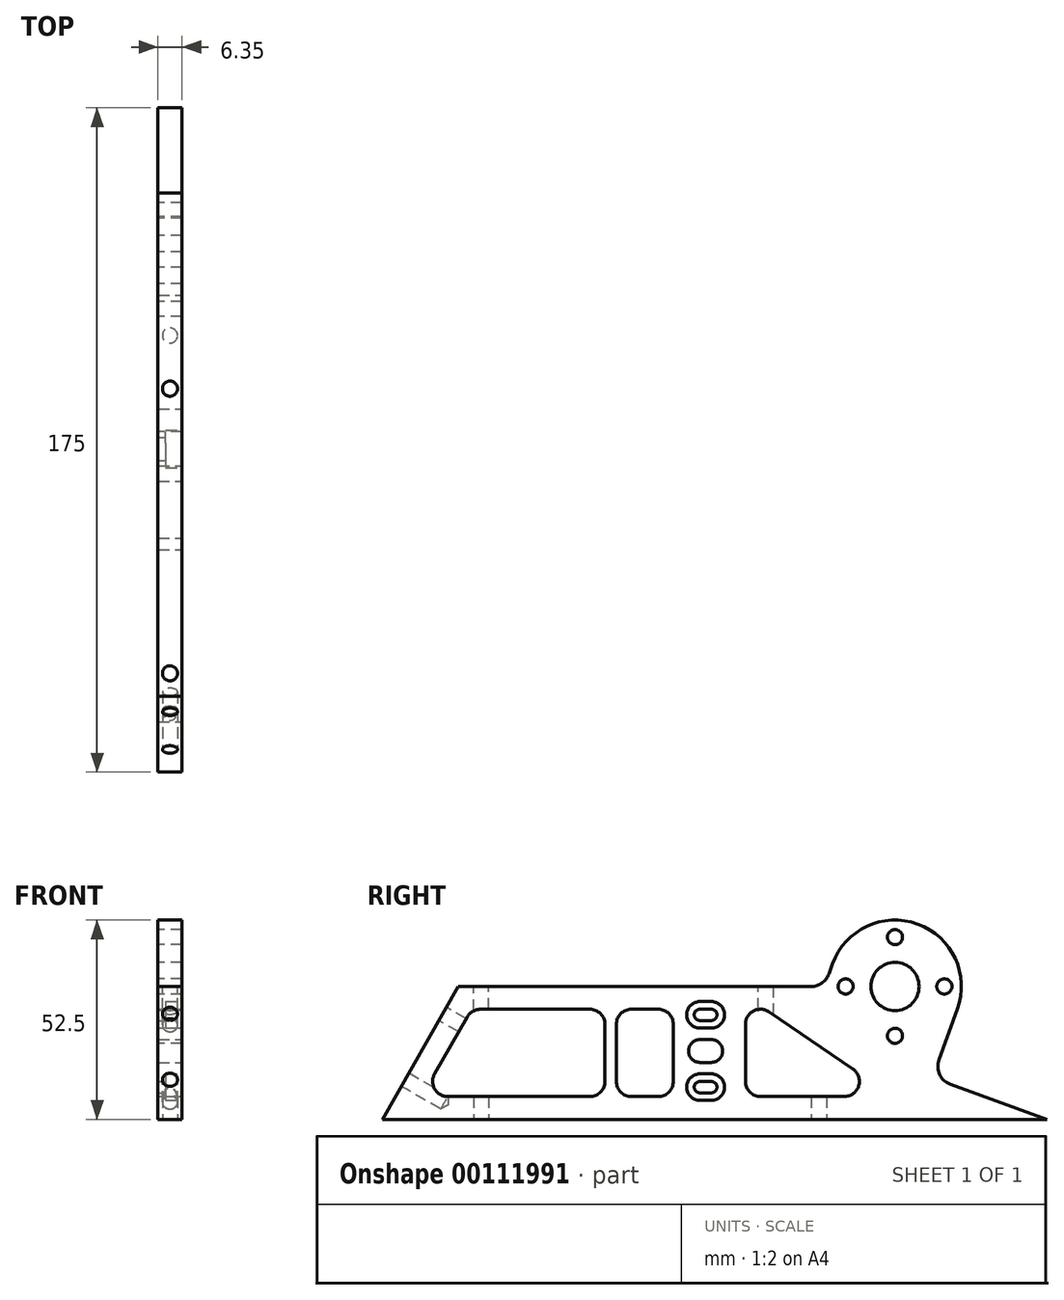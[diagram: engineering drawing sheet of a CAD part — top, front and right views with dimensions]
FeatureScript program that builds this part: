
annotation { "Feature Type Name" : "Feature", "Feature Type Description" : "" }
export const myFeature = defineFeature(function(context is Context, id is Id, definition is map)
    precondition{}
    {
        {
            var Q0;
            Q0=qCreatedBy(makeId("Right.planeOp"),FACE);
            var sketch = newSketch(context, id + "F0", { "sketchPlane" : qUnion([Q0])});
            skLineSegment(sketch, "E0", {"start": v(0, 0) * mm, "end": v(-30.13, 10.96) * mm});
            skLineSegment(sketch, "E1", {"start": v(-58.62, 35) * mm, "end": v(-155, 35) * mm});
            skLineSegment(sketch, "E2", {"start": v(-155, 35) * mm, "end": v(-175, 0) * mm});
            skLineSegment(sketch, "E3", {"start": v(-175, 0) * mm, "end": v(0, 0) * mm});
            skCircle(sketch, "E4", {"center": v(-88.38, 18) * mm, "radius": 14 * mm, "construction": true});
            skCircle(sketch, "E5", {"center": v(-40, 35) * mm, "radius": 34.3 * mm, "construction": true});
            skCircle(sketch, "E6", {"center": v(-130, 17.5) * mm, "radius": 11 * mm, "construction": true});
            skCircle(sketch, "E7", {"center": v(-40, 35) * mm, "radius": 6.35 * mm});
            skCircle(sketch, "E8", {"center": v(-40, 35) * mm, "radius": 13 * mm, "construction": true});
            skCircle(sketch, "E9", {"center": v(-40, 48) * mm, "radius": 2 * mm});
            skCircle(sketch, "E10", {"center": v(-53, 35) * mm, "radius": 2 * mm});
            skCircle(sketch, "E11", {"center": v(-27, 35) * mm, "radius": 2 * mm});
            skCircle(sketch, "E12", {"center": v(-40, 22) * mm, "radius": 2 * mm});
            skCircle(sketch, "E13", {"center": v(-130, 17.5) * mm, "radius": 25.4 * mm, "construction": true});
            skLineSegment(sketch, "E14", {"start": v(-130, 17.5) * mm, "end": v(-130, 35) * mm, "construction": true});
            skLineSegment(sketch, "E15", {"start": v(-130, 17.5) * mm, "end": v(-130, 0) * mm, "construction": true});
            skLineSegment(sketch, "E16", {"start": v(-58.62, 35) * mm, "end": v(-56.44, 40.99) * mm});
            skArc(sketch, "E17", {"start": v(-23.56, 29.01) * mm, "mid": v(-34.01, 51.44) * mm, "end": v(-56.44, 40.99) * mm});
            skLineSegment(sketch, "E18", {"start": v(-23.56, 29.01) * mm, "end": v(-30.13, 10.96) * mm});
            skPoint(sketch, "E19.orphan", {"position": v(-75, 35) * mm});
            skCircle(sketch, "E20", {"center": v(-130, 17.5) * mm, "radius": 2 * mm});
            skCircle(sketch, "E21", {"center": v(-88.38, 18) * mm, "radius": 3 * mm});
            skSolve(sketch);
        }
        {
            var Q0;
            Q0 = qSketchRegion(id + "F0", true);
            extrude(context, id + "F1", {"entities" : qUnion([Q0]), "depth" : 6.35 * mm});
        }
        {
            var Q0;
            Q0=makeQuery(id+"F1.opExtrude","SWEPT_EDGE",EDGE,{"disambiguationData":[OSD([sQuery(id+"F0.wireOp",EDGE,"E1"),sQuery(id+"F0.wireOp",EDGE,"E16")])]});
            var Q1;
            Q1=makeQuery(id+"F1.opExtrude","SWEPT_EDGE",EDGE,{"disambiguationData":[OSD([sQuery(id+"F0.wireOp",EDGE,"E0"),sQuery(id+"F0.wireOp",EDGE,"E18")])]});
            fillet(context, id + "F2", {"entities" : qUnion([Q0, Q1]), "radius" : 5 * mm, "tangentPropagation" : true, "allowEdgeOverflow" : false});
        }
        {
            var Q0;
            Q0=makeQuery(id+"F1.opExtrude","CAP_FACE",FACE,{"disambiguationData":[OSD([sQuery(id+"F0.wireOp",EDGE,"E0"),sQuery(id+"F0.wireOp",EDGE,"E1"),sQuery(id+"F0.wireOp",EDGE,"E2"),sQuery(id+"F0.wireOp",EDGE,"E3"),sQuery(id+"F0.wireOp",EDGE,"E7"),sQuery(id+"F0.wireOp",EDGE,"E9"),sQuery(id+"F0.wireOp",EDGE,"E10"),sQuery(id+"F0.wireOp",EDGE,"E11"),sQuery(id+"F0.wireOp",EDGE,"E12"),sQuery(id+"F0.wireOp",EDGE,"E16"),sQuery(id+"F0.wireOp",EDGE,"E17"),sQuery(id+"F0.wireOp",EDGE,"E18"),sQuery(id+"F0.wireOp",EDGE,"E20"),sQuery(id+"F0.wireOp",EDGE,"E21")])],"isStart":false});
            var sketch = newSketch(context, id + "F3", { "sketchPlane" : qUnion([Q0])});
            skCircle(sketch, "E22", {"center": v(-88.38, 18) * mm, "radius": 9.53 * mm, "construction": true});
            skArc(sketch, "E23", {"start": v(-91.38, 29.03) * mm, "mid": v(-92.88, 27.53) * mm, "end": v(-91.38, 26.03) * mm});
            skArc(sketch, "E24", {"start": v(-91.38, 9.98) * mm, "mid": v(-92.88, 8.48) * mm, "end": v(-91.38, 6.98) * mm});
            skArc(sketch, "E25", {"start": v(-91.38, 21) * mm, "mid": v(-94.38, 18) * mm, "end": v(-91.38, 15) * mm});
            skLineSegment(sketch, "E26", {"start": v(-91.38, 29.03) * mm, "end": v(-88.38, 29.03) * mm});
            skLineSegment(sketch, "E27", {"start": v(-91.38, 21) * mm, "end": v(-88.38, 21) * mm});
            skLineSegment(sketch, "E28", {"start": v(-91.38, 15) * mm, "end": v(-88.38, 15) * mm});
            skLineSegment(sketch, "E29", {"start": v(-91.38, 9.98) * mm, "end": v(-88.38, 9.98) * mm});
            skLineSegment(sketch, "E30", {"start": v(-91.38, 6.98) * mm, "end": v(-88.38, 6.98) * mm});
            skLineSegment(sketch, "E31", {"start": v(-91.38, 26.03) * mm, "end": v(-88.38, 26.03) * mm});
            skArc(sketch, "E32.trimOffspring", {"start": v(-88.38, 26.03) * mm, "mid": v(-86.88, 27.53) * mm, "end": v(-88.38, 29.03) * mm});
            skArc(sketch, "E33.trimOffspring", {"start": v(-88.38, 6.98) * mm, "mid": v(-86.88, 8.48) * mm, "end": v(-88.38, 9.98) * mm});
            skArc(sketch, "E34", {"start": v(-88.38, 15) * mm, "mid": v(-85.38, 18) * mm, "end": v(-88.38, 21) * mm});
            skSolve(sketch);
        }
        {
            var Q0;
            Q0 = qSketchRegion(id + "F3", true);
            extrude(context, id + "F4", {"entities" : qUnion([Q0]), "operationType" : NewBodyOperationType.REMOVE, "endBound" : BoundingType.THROUGH_ALL, "oppositeDirection" : true, "depth" : 25 * mm});
        }
        {
            var Q0;
            Q0=makeQuery(id+"F1.opExtrude","CAP_FACE",FACE,{"disambiguationData":[OSD([sQuery(id+"F0.wireOp",EDGE,"E0"),sQuery(id+"F0.wireOp",EDGE,"E1"),sQuery(id+"F0.wireOp",EDGE,"E2"),sQuery(id+"F0.wireOp",EDGE,"E3"),sQuery(id+"F0.wireOp",EDGE,"E7"),sQuery(id+"F0.wireOp",EDGE,"E9"),sQuery(id+"F0.wireOp",EDGE,"E10"),sQuery(id+"F0.wireOp",EDGE,"E11"),sQuery(id+"F0.wireOp",EDGE,"E12"),sQuery(id+"F0.wireOp",EDGE,"E16"),sQuery(id+"F0.wireOp",EDGE,"E17"),sQuery(id+"F0.wireOp",EDGE,"E18"),sQuery(id+"F0.wireOp",EDGE,"E20"),sQuery(id+"F0.wireOp",EDGE,"E21")])],"isStart":false});
            var sketch = newSketch(context, id + "F5", { "sketchPlane" : qUnion([Q0])});
            skLineSegment(sketch, "E35.0", {"start": v(-91.38, 31.03) * mm, "end": v(-88.38, 31.03) * mm});
            skArc(sketch, "E35.1", {"start": v(-91.38, 31.03) * mm, "mid": v(-94.88, 27.53) * mm, "end": v(-91.38, 24.03) * mm});
            skLineSegment(sketch, "E35.2", {"start": v(-91.38, 24.03) * mm, "end": v(-88.38, 24.03) * mm});
            skArc(sketch, "E35.3", {"start": v(-88.38, 24.03) * mm, "mid": v(-84.88, 27.53) * mm, "end": v(-88.38, 31.03) * mm});
            skLineSegment(sketch, "E36.0", {"start": v(-91.38, 11.98) * mm, "end": v(-88.38, 11.98) * mm});
            skArc(sketch, "E36.1", {"start": v(-91.38, 11.98) * mm, "mid": v(-94.88, 8.48) * mm, "end": v(-91.38, 4.98) * mm});
            skLineSegment(sketch, "E36.2", {"start": v(-91.38, 4.98) * mm, "end": v(-88.38, 4.98) * mm});
            skArc(sketch, "E36.3", {"start": v(-88.38, 4.98) * mm, "mid": v(-84.88, 8.48) * mm, "end": v(-88.38, 11.98) * mm});
            skSolve(sketch);
        }
        {
            var Q0;
            Q0 = qSketchRegion(id + "F5", true);
            extrude(context, id + "F6", {"entities" : qUnion([Q0]), "operationType" : NewBodyOperationType.REMOVE, "oppositeDirection" : true, "depth" : 4.35 * mm});
        }
        {
            var Q0;
            Q0=makeQuery(id+"F1.opExtrude","CAP_FACE",FACE,{"disambiguationData":[OSD([sQuery(id+"F0.wireOp",EDGE,"E0"),sQuery(id+"F0.wireOp",EDGE,"E1"),sQuery(id+"F0.wireOp",EDGE,"E2"),sQuery(id+"F0.wireOp",EDGE,"E3"),sQuery(id+"F0.wireOp",EDGE,"E7"),sQuery(id+"F0.wireOp",EDGE,"E9"),sQuery(id+"F0.wireOp",EDGE,"E10"),sQuery(id+"F0.wireOp",EDGE,"E11"),sQuery(id+"F0.wireOp",EDGE,"E12"),sQuery(id+"F0.wireOp",EDGE,"E16"),sQuery(id+"F0.wireOp",EDGE,"E17"),sQuery(id+"F0.wireOp",EDGE,"E18"),sQuery(id+"F0.wireOp",EDGE,"E20"),sQuery(id+"F0.wireOp",EDGE,"E21")])],"isStart":false});
            var sketch = newSketch(context, id + "F7", { "sketchPlane" : qUnion([Q0])});
            skPoint(sketch, "E37", {"position": v(-130, 17.5) * mm});
            skLineSegment(sketch, "E38", {"start": v(-79.38, 25) * mm, "end": v(-79.38, 10) * mm});
            skLineSegment(sketch, "E39", {"start": v(-75.38, 6) * mm, "end": v(-53.38, 6) * mm});
            skLineSegment(sketch, "E40", {"start": v(-51.13, 13.3) * mm, "end": v(-73.13, 28.3) * mm});
            skPoint(sketch, "E41.visualSharp", {"position": v(-79.38, 32.57) * mm});
            skArc(sketch, "E41.filletArc", {"start": v(-73.13, 28.3) * mm, "mid": v(-77.25, 28.54) * mm, "end": v(-79.38, 25) * mm});
            skPoint(sketch, "E42.visualSharp", {"position": v(-40.41, 6) * mm});
            skArc(sketch, "E42.filletArc", {"start": v(-53.38, 6) * mm, "mid": v(-49.56, 8.82) * mm, "end": v(-51.13, 13.3) * mm});
            skPoint(sketch, "E43.visualSharp", {"position": v(-79.38, 6) * mm});
            skArc(sketch, "E43.filletArc", {"start": v(-79.38, 10) * mm, "mid": v(-78.2, 7.17) * mm, "end": v(-75.38, 6) * mm});
            skSolve(sketch);
        }
        {
            var Q0;
            Q0 = qSketchRegion(id + "F7", true);
            extrude(context, id + "F8", {"entities" : qUnion([Q0]), "operationType" : NewBodyOperationType.REMOVE, "endBound" : BoundingType.THROUGH_ALL, "oppositeDirection" : true, "depth" : 25 * mm});
        }
        {
            var Q0;
            Q0=makeQuery(id+"F1.opExtrude","CAP_FACE",FACE,{"disambiguationData":[OSD([sQuery(id+"F0.wireOp",EDGE,"E0"),sQuery(id+"F0.wireOp",EDGE,"E1"),sQuery(id+"F0.wireOp",EDGE,"E2"),sQuery(id+"F0.wireOp",EDGE,"E3"),sQuery(id+"F0.wireOp",EDGE,"E7"),sQuery(id+"F0.wireOp",EDGE,"E9"),sQuery(id+"F0.wireOp",EDGE,"E10"),sQuery(id+"F0.wireOp",EDGE,"E11"),sQuery(id+"F0.wireOp",EDGE,"E12"),sQuery(id+"F0.wireOp",EDGE,"E16"),sQuery(id+"F0.wireOp",EDGE,"E17"),sQuery(id+"F0.wireOp",EDGE,"E18"),sQuery(id+"F0.wireOp",EDGE,"E20"),sQuery(id+"F0.wireOp",EDGE,"E21")])],"isStart":false});
            var sketch = newSketch(context, id + "F9", { "sketchPlane" : qUnion([Q0])});
            skLineSegment(sketch, "E44.bottom", {"start": v(-113.38, 29) * mm, "end": v(-98.38, 29) * mm});
            skLineSegment(sketch, "E44.top", {"start": v(-113.38, 6) * mm, "end": v(-98.38, 6) * mm});
            skLineSegment(sketch, "E44.left", {"start": v(-113.38, 29) * mm, "end": v(-113.38, 6) * mm});
            skLineSegment(sketch, "E44.right", {"start": v(-98.38, 29) * mm, "end": v(-98.38, 6) * mm});
            skLineSegment(sketch, "E45.bottom", {"start": v(-116.38, 29) * mm, "end": v(-151.52, 29) * mm});
            skLineSegment(sketch, "E45.top", {"start": v(-116.38, 6) * mm, "end": v(-164.66, 6) * mm});
            skLineSegment(sketch, "E45.left", {"start": v(-116.38, 29) * mm, "end": v(-116.38, 6) * mm});
            skLineSegment(sketch, "E45.right", {"start": v(-151.52, 29) * mm, "end": v(-164.66, 6) * mm});
            skSolve(sketch);
        }
        {
            var Q0;
            Q0 = qSketchRegion(id + "F9", true);
            extrude(context, id + "F10", {"entities" : qUnion([Q0]), "operationType" : NewBodyOperationType.REMOVE, "endBound" : BoundingType.THROUGH_ALL, "oppositeDirection" : true, "depth" : 25 * mm});
        }
        {
            var Q0;
            Q0=makeQuery(id+"F10.boolean.opBoolean","COPY",EDGE,{"derivedFrom":makeQuery(id+"F10.opExtrude","SWEPT_EDGE",EDGE,{"disambiguationData":[OSD([sQuery(id+"F9.wireOp",EDGE,"E45.bottom"),sQuery(id+"F9.wireOp",EDGE,"E45.left")])]})});
            var Q1;
            Q1=makeQuery(id+"F10.boolean.opBoolean","COPY",EDGE,{"derivedFrom":makeQuery(id+"F10.opExtrude","SWEPT_EDGE",EDGE,{"disambiguationData":[OSD([sQuery(id+"F9.wireOp",EDGE,"E44.bottom"),sQuery(id+"F9.wireOp",EDGE,"E44.right")])]})});
            var Q2;
            Q2=makeQuery(id+"F10.boolean.opBoolean","COPY",EDGE,{"derivedFrom":makeQuery(id+"F10.opExtrude","SWEPT_EDGE",EDGE,{"disambiguationData":[OSD([sQuery(id+"F9.wireOp",EDGE,"E45.top"),sQuery(id+"F9.wireOp",EDGE,"E45.left")])]})});
            var Q3;
            Q3=makeQuery(id+"F10.boolean.opBoolean","COPY",EDGE,{"derivedFrom":makeQuery(id+"F10.opExtrude","SWEPT_EDGE",EDGE,{"disambiguationData":[OSD([sQuery(id+"F9.wireOp",EDGE,"E44.top"),sQuery(id+"F9.wireOp",EDGE,"E44.right")])]})});
            var Q4;
            Q4=makeQuery(id+"F10.boolean.opBoolean","COPY",EDGE,{"derivedFrom":makeQuery(id+"F10.opExtrude","SWEPT_EDGE",EDGE,{"disambiguationData":[OSD([sQuery(id+"F9.wireOp",EDGE,"E44.top"),sQuery(id+"F9.wireOp",EDGE,"E44.left")])]})});
            var Q5;
            Q5=makeQuery(id+"F10.boolean.opBoolean","COPY",EDGE,{"derivedFrom":makeQuery(id+"F10.opExtrude","SWEPT_EDGE",EDGE,{"disambiguationData":[OSD([sQuery(id+"F9.wireOp",EDGE,"E45.top"),sQuery(id+"F9.wireOp",EDGE,"E45.right")])]})});
            var Q6;
            Q6=makeQuery(id+"F10.boolean.opBoolean","COPY",EDGE,{"derivedFrom":makeQuery(id+"F10.opExtrude","SWEPT_EDGE",EDGE,{"disambiguationData":[OSD([sQuery(id+"F9.wireOp",EDGE,"E45.bottom"),sQuery(id+"F9.wireOp",EDGE,"E45.right")])]})});
            var Q7;
            Q7=makeQuery(id+"F10.boolean.opBoolean","COPY",EDGE,{"derivedFrom":makeQuery(id+"F10.opExtrude","SWEPT_EDGE",EDGE,{"disambiguationData":[OSD([sQuery(id+"F9.wireOp",EDGE,"E44.bottom"),sQuery(id+"F9.wireOp",EDGE,"E44.left")])]})});
            fillet(context, id + "F11", {"entities" : qUnion([Q0, Q1, Q2, Q3, Q4, Q5, Q6, Q7]), "radius" : 4 * mm, "tangentPropagation" : true, "allowEdgeOverflow" : false});
        }
        {
            var Q0;
            Q0=makeQuery(id+"F1.opExtrude","SWEPT_FACE",FACE,{"disambiguationData":[OSD([sQuery(id+"F0.wireOp",EDGE,"E1")])]});
            var sketch = newSketch(context, id + "F12", { "sketchPlane" : qUnion([Q0])});
            skPoint(sketch, "E46", {"position": v(3.17, -74) * mm});
            skPoint(sketch, "E47", {"position": v(3.17, -149) * mm});
            skPoint(sketch, "E48", {"position": v(3.17, -155) * mm});
            skSolve(sketch);
        }
        {
            var Q0;
            Q0=sQuery(id+"F12.wireOp",VERTEX,"E46");
            var Q1;
            Q1=sQuery(id+"F12.wireOp",VERTEX,"E47");
            var Q2;
            Q2=makeQuery(id+"F1.opExtrude","SWEPT_BODY",BODY,{"disambiguationData":[OSD([sQuery(id+"F0.wireOp",EDGE,"E0"),sQuery(id+"F0.wireOp",EDGE,"E1"),sQuery(id+"F0.wireOp",EDGE,"E2"),sQuery(id+"F0.wireOp",EDGE,"E3"),sQuery(id+"F0.wireOp",EDGE,"E7"),sQuery(id+"F0.wireOp",EDGE,"E9"),sQuery(id+"F0.wireOp",EDGE,"E10"),sQuery(id+"F0.wireOp",EDGE,"E11"),sQuery(id+"F0.wireOp",EDGE,"E12"),sQuery(id+"F0.wireOp",EDGE,"E16"),sQuery(id+"F0.wireOp",EDGE,"E17"),sQuery(id+"F0.wireOp",EDGE,"E18"),sQuery(id+"F0.wireOp",EDGE,"E20"),sQuery(id+"F0.wireOp",EDGE,"E21")])]});
            hole(context, id + "F13", {"style" : HoleStyle.SIMPLE, "endStyle" : HoleEndStyle.BLIND, "holeDiameter" : 4 * mm, "holeDepth" : 12 * mm, "locations" : qUnion([Q0, Q1]), "scope" : qUnion([Q2])});
        }
        {
            var Q0;
            Q0=makeQuery(id+"F1.opExtrude","SWEPT_FACE",FACE,{"disambiguationData":[OSD([sQuery(id+"F0.wireOp",EDGE,"E2")])]});
            var sketch = newSketch(context, id + "F14", { "sketchPlane" : qUnion([Q0])});
            skPoint(sketch, "E49", {"position": v(3.17, -86.82) * mm});
            skPoint(sketch, "E50", {"position": v(3.17, -74.82) * mm});
            skPoint(sketch, "E51", {"position": v(3.17, -54.82) * mm});
            skSolve(sketch);
        }
        {
            var Q0;
            Q0=sQuery(id+"F14.wireOp",VERTEX,"E51");
            var Q1;
            Q1=sQuery(id+"F14.wireOp",VERTEX,"E50");
            var Q2;
            Q2=makeQuery(id+"F1.opExtrude","SWEPT_BODY",BODY,{"disambiguationData":[OSD([sQuery(id+"F0.wireOp",EDGE,"E0"),sQuery(id+"F0.wireOp",EDGE,"E1"),sQuery(id+"F0.wireOp",EDGE,"E2"),sQuery(id+"F0.wireOp",EDGE,"E3"),sQuery(id+"F0.wireOp",EDGE,"E7"),sQuery(id+"F0.wireOp",EDGE,"E9"),sQuery(id+"F0.wireOp",EDGE,"E10"),sQuery(id+"F0.wireOp",EDGE,"E11"),sQuery(id+"F0.wireOp",EDGE,"E12"),sQuery(id+"F0.wireOp",EDGE,"E16"),sQuery(id+"F0.wireOp",EDGE,"E17"),sQuery(id+"F0.wireOp",EDGE,"E18"),sQuery(id+"F0.wireOp",EDGE,"E20"),sQuery(id+"F0.wireOp",EDGE,"E21")])]});
            hole(context, id + "F15", {"style" : HoleStyle.SIMPLE, "endStyle" : HoleEndStyle.BLIND, "holeDiameter" : 4 * mm, "holeDepth" : 12 * mm, "locations" : qUnion([Q0, Q1]), "scope" : qUnion([Q2])});
        }
        {
            var Q0;
            Q0=makeQuery(id+"F1.opExtrude","SWEPT_FACE",FACE,{"disambiguationData":[OSD([sQuery(id+"F0.wireOp",EDGE,"E3")])]});
            var sketch = newSketch(context, id + "F16", { "sketchPlane" : qUnion([Q0])});
            skPoint(sketch, "E52", {"position": v(3.17, 175) * mm});
            skPoint(sketch, "E53", {"position": v(3.18, 149) * mm});
            skPoint(sketch, "E54", {"position": v(3.18, 60) * mm});
            skSolve(sketch);
        }
        {
            var Q0;
            Q0=sQuery(id+"F16.wireOp",VERTEX,"E53");
            var Q1;
            Q1=sQuery(id+"F16.wireOp",VERTEX,"E54");
            var Q2;
            Q2=makeQuery(id+"F1.opExtrude","SWEPT_BODY",BODY,{"disambiguationData":[OSD([sQuery(id+"F0.wireOp",EDGE,"E0"),sQuery(id+"F0.wireOp",EDGE,"E1"),sQuery(id+"F0.wireOp",EDGE,"E2"),sQuery(id+"F0.wireOp",EDGE,"E3"),sQuery(id+"F0.wireOp",EDGE,"E7"),sQuery(id+"F0.wireOp",EDGE,"E9"),sQuery(id+"F0.wireOp",EDGE,"E10"),sQuery(id+"F0.wireOp",EDGE,"E11"),sQuery(id+"F0.wireOp",EDGE,"E12"),sQuery(id+"F0.wireOp",EDGE,"E16"),sQuery(id+"F0.wireOp",EDGE,"E17"),sQuery(id+"F0.wireOp",EDGE,"E18"),sQuery(id+"F0.wireOp",EDGE,"E20"),sQuery(id+"F0.wireOp",EDGE,"E21")])]});
            hole(context, id + "F17", {"style" : HoleStyle.SIMPLE, "endStyle" : HoleEndStyle.BLIND, "holeDiameter" : 4 * mm, "holeDepth" : 12 * mm, "locations" : qUnion([Q0, Q1]), "scope" : qUnion([Q2])});
        }
    });
